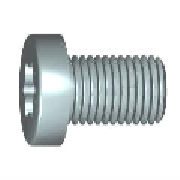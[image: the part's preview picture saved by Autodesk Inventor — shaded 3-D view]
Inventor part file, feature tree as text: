
AUTODESK INVENTOR PART (.ipt)
format: ipt  version: 2022 (Build 260153000, 153)  size: 216,064 bytes
history: native  units: mm
features: fillet x4, sketch x2, revolve x1, thread x1, extrude x1, pattern_circular x1, chamfer x1
ambient origin geometry x8: Origin, YZ Plane, XZ Plane, XY Plane, X Axis, Y Axis, Z Axis, Center Point
bodies: Solid1 (feature_tree)
feature tree (11):
  revolve  "Revolution1"  [1 undecoded]
  thread  "Thread1"  [1 undecoded]
  extrude  "Extrusion1"  TaperAngle=90.0deg  [1 undecoded]
  pattern_circular  "Circular Pattern1"  [2 undecoded]
  fillet  "Fillet2"  [1 undecoded]
  fillet  "Fillet3"  [1 undecoded]
  fillet  "Fillet4"  Radius=5.6mm
  fillet  "Fillet5"  Radius=3.92mm
  chamfer  "Chamfer2"  Distance=2.42mm
  sketch  "Sketch1"  dims[d0=6.0mm d1=10.0mm d2=6.0mm]
  sketch  "Sketch2"  dims[d3=25.0mm d4=90.0deg d6=25.0mm d7=0.0mm d19=60.0deg d20=30.0deg d21=5.6mm d26=3.92mm d27=2.42mm d28=0.0mm d29=60.0mm d30=360.0deg d32=0.6mm d33=0.6mm d34=0.6mm d35=0.1mm d36=0.6mm d37=2.0mm d38=45.0deg d42=0.0mm d43=0.0mm d44=0.0mm]
note: 7 required parameter values undecoded (feature->parameter linkage not recoverable at this tier; creation-order binding heuristic only, values carry confidence <= 0.55)